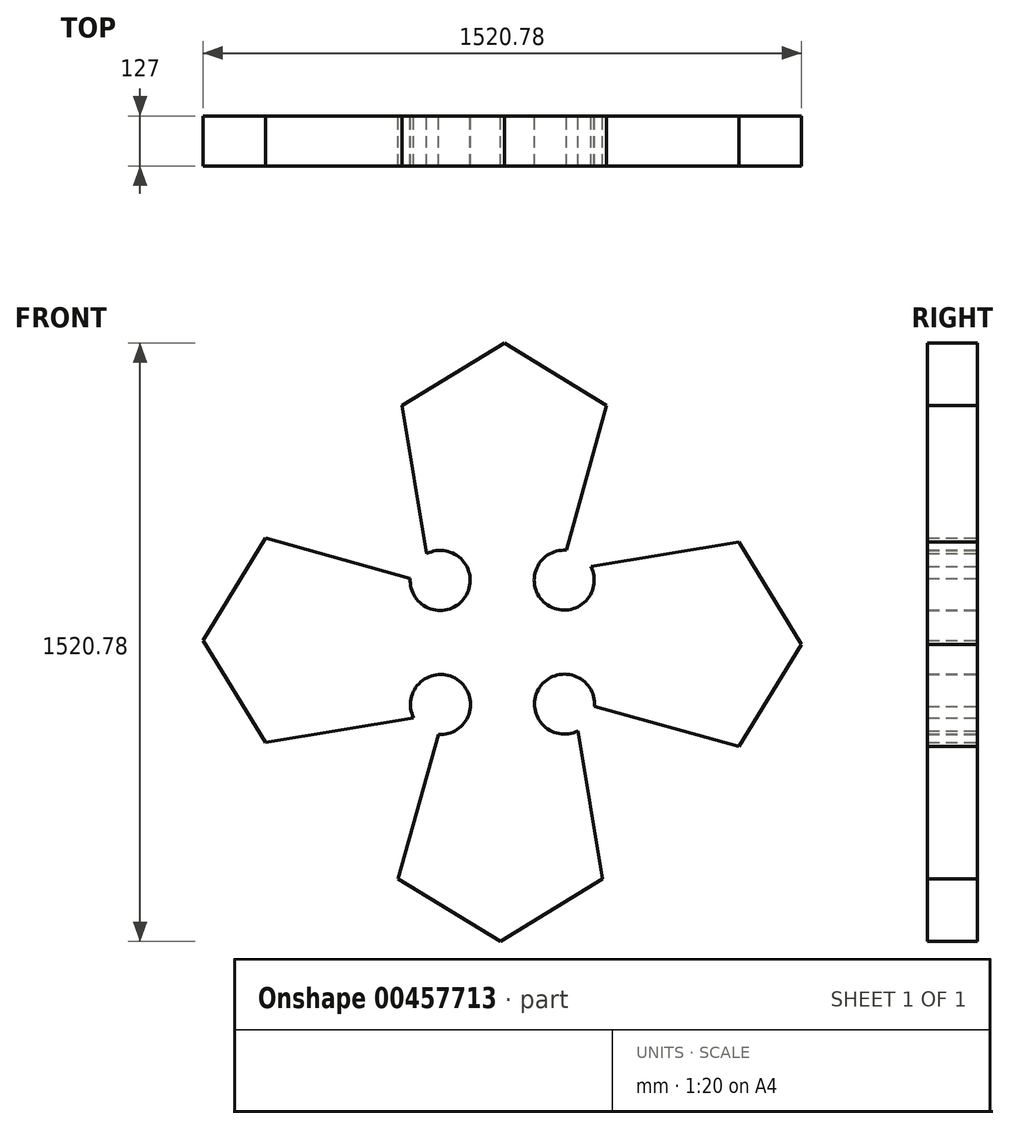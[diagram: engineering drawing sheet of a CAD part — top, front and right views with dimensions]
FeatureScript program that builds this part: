
annotation { "Feature Type Name" : "Feature", "Feature Type Description" : "" }
export const myFeature = defineFeature(function(context is Context, id is Id, definition is map)
    precondition{}
    {
        {
            var Q0;
            Q0=qCreatedBy(makeId("Front.planeOp"),FACE);
            var sketch = newSketch(context, id + "F0", { "sketchPlane" : qUnion([Q0])});
            skLineSegment(sketch, "E0", {"start": v(157.66, 235.6) * mm, "end": v(259.82, 602.64) * mm});
            skLineSegment(sketch, "E1", {"start": v(259.82, 602.64) * mm, "end": v(0, 762) * mm});
            skLineSegment(sketch, "E2", {"start": v(0, 762) * mm, "end": v(-259.82, 602.64) * mm});
            skLineSegment(sketch, "E3", {"start": v(-259.82, 602.64) * mm, "end": v(-197.29, 226.8) * mm});
            skArc(sketch, "E4.MirrorC", {"start": v(157.66, 235.6) * mm, "mid": v(109.97, 96.2) * mm, "end": v(220.22, 193.92) * mm});
            skLineSegment(sketch, "E5.trimOffspring", {"start": v(150.32, 235.77) * mm, "end": v(157.66, 235.6) * mm});
            skArc(sketch, "E6.1.0", {"start": v(-167.62, -232.37) * mm, "mid": v(-119.9, -92.95) * mm, "end": v(-230.18, -190.7) * mm});
            skArc(sketch, "E6.1.1", {"start": v(-238.96, 164.25) * mm, "mid": v(-99.58, 116.56) * mm, "end": v(-197.29, 226.8) * mm});
            skLineSegment(sketch, "E6.1.2", {"start": v(-238.96, 164.25) * mm, "end": v(-606, 266.41) * mm});
            skLineSegment(sketch, "E6.1.3", {"start": v(-606, 266.41) * mm, "end": v(-765.37, 6.6) * mm});
            skLineSegment(sketch, "E6.1.4", {"start": v(-765.37, 6.6) * mm, "end": v(-606, -253.23) * mm});
            skLineSegment(sketch, "E6.1.5", {"start": v(-606, -253.23) * mm, "end": v(-230.18, -190.7) * mm});
            skArc(sketch, "E6.2.0", {"start": v(229, -161.03) * mm, "mid": v(89.58, -113.31) * mm, "end": v(187.33, -223.58) * mm});
            skLineSegment(sketch, "E6.2.2", {"start": v(-167.62, -232.37) * mm, "end": v(-269.78, -599.42) * mm});
            skLineSegment(sketch, "E6.2.3", {"start": v(-269.78, -599.42) * mm, "end": v(-9.96, -758.78) * mm});
            skLineSegment(sketch, "E6.2.4", {"start": v(-9.96, -758.78) * mm, "end": v(249.86, -599.42) * mm});
            skLineSegment(sketch, "E6.2.5", {"start": v(249.86, -599.42) * mm, "end": v(187.33, -223.58) * mm});
            skLineSegment(sketch, "E6.3.2", {"start": v(229, -161.03) * mm, "end": v(596.05, -263.2) * mm});
            skLineSegment(sketch, "E6.3.3", {"start": v(596.05, -263.2) * mm, "end": v(755.4, -3.37) * mm});
            skLineSegment(sketch, "E6.3.4", {"start": v(755.4, -3.37) * mm, "end": v(596.05, 256.45) * mm});
            skLineSegment(sketch, "E6.3.5", {"start": v(596.05, 256.45) * mm, "end": v(220.22, 193.92) * mm});
            skPoint(sketch, "E6.center", {"position": v(-4.98, 1.61) * mm});
            skSolve(sketch);
        }
        {
            var Q0;
            {var subQ4=sQuery(id+"F0.wireOp",EDGE,"E0");Q0=makeQuery(id+"F0.imprint","IMPRINT",FACE,{"disambiguationData":[TD([[makeQuery(id+"F0.imprint","IMPRINT",EDGE,{"derivedFrom":subQ4}),1.0]])]});}
            extrude(context, id + "F1", {"entities" : qUnion([Q0]), "depth" : 127 * mm});
        }
    });
